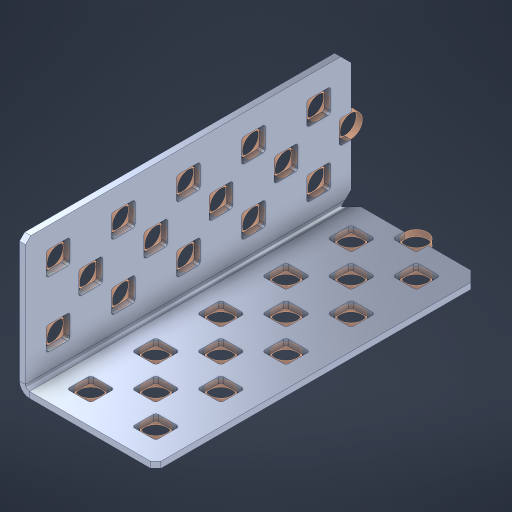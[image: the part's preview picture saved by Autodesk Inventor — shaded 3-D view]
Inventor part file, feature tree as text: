
AUTODESK INVENTOR PART (.ipt)
format: ipt  version: 2023 (Build 270158000, 158)  size: 677,376 bytes
history: native  units: in
note: dims shown in document units (in); Inventor stores cm internally (conversion verified against a paired STEP export)
features: other x36, extrude x28, sheet_metal_op x8, sketch x7, pattern_linear x2, mirror x1, chamfer x1
ambient origin geometry x8: Origin, YZ Plane, XZ Plane, XY Plane, X Axis, Y Axis, Z Axis, Center Point
bodies: Solid1 (feature_tree), Body (feature_tree)
feature tree (83):
  sheet_metal_op  "Flanges"
  sheet_metal_op  "Body Pattern"
  pattern_linear  "Center Pattern"  Spacing1=1.0in  [1 undecoded]
  other  "Arc Length"
  pattern_linear  "Notch Pattern"  Spacing1=0.1875in  [1 undecoded]
  other  "Diagonal Plane"
  mirror  "Everything Mirrored"
  chamfer  "End Chamfer"
  sketch  "Sketch1"  dims[d0=1.0in]
  other  "Plate1"
  sketch  "Sketch2"  dims[d1=2.5in]
  other  "Plate2"
  sheet_metal_op  "Bend1"
  sheet_metal_op  "Corner1"
  sketch  "Sketch8"  dims[d2=0.0469in]
  sketch  "Sketch9"  dims[d3=0.0469in]
  other  "Srf91"
  sheet_metal_op  "Body Pattern Sketch"
  other  "Srf92"
  sketch  "Sketch13"  dims[d4=0.0234in]
  sketch  "Sketch15"  dims[d5=0.0938in]
  sketch  "Sketch16"  dims[d6=0.0469in d7=1.0in d8=90.0deg d9=0.0312in d10=0.1875in d11=0.0469in d12=0.0469in d49=0.182in d50=0.02in d52=0.25in d53=0.0469in d54=0.0in d55=0.172in d56=1.0in d57=0.0in d60=1.9685in d62=0.5in d63=0.7874in d65=0.5in d85=0.1473in d86=0.1659in d89=0.0469in d90=0.0in d91=0.04in d92=0.0491in d95=2.5in d96=0.04in d97=0.25in d98=45.0deg d99=0.25in d106=0.182in d107=0.02in d108=0.5in d110=0.0469in d111=0.0in d112=0.172in d113=0.5in d114=0.0in d117=0.5in d123=0.25in d125=0.25in d126=0.0491in d127=0.1227in d128=0.08in d129=0.04in d130=2.5in]
  other  "Srf786"
  other  "Srf856"
  other  "Srf857"
  other  "Srf858"
  other  "Srf859"
  other  "Srf860"
  other  "Srf861"
  other  "Srf889"
  other  "Srf890"
  other  "Srf891"
  other  "Srf1275"
  other  "Srf1276"
  other  "Srf1278"
  other  "Srf1279"
  other  "Srf1280"
  other  "Srf1281"
  other  "Srf1282"
  other  "Srf1283"
  other  "Srf1277"
  other  "Srf1285"
  other  "Srf1286"
  other  "Srf1287"
  other  "Srf1383"
  other  "Srf1384"
  other  "Srf1445"
  other  "Srf1475"
  other  "Srf1476"
  other  "Srf1537"
  sheet_metal_op  "Body Stamp"
  sheet_metal_op  "Body Circle"
  other  "Center Stamp"
  other  "Center Circle"
  sheet_metal_op  "Notch"
  extrude  "ExtrusionSrf92"  Depth=0.0469in
  extrude  "ExtrusionSrf856"  Depth=0.0469in
  extrude  "ExtrusionSrf857"  Depth=2.5in
  extrude  "ExtrusionSrf858"  Depth=0.02in
  extrude  "ExtrusionSrf859"  Depth=2.5in
  extrude  "ExtrusionSrf860"  Depth=0.0469in
  extrude  "ExtrusionSrf861"  TaperAngle=0.0deg  [1 undecoded]
  extrude  "ExtrusionSrf889"  Depth=2.5in
  extrude  "ExtrusionSrf890"  Depth=1.0in TaperAngle=0.0deg
  extrude  "ExtrusionSrf891"  Depth=2.5in
  extrude  "ExtrusionSrf1275"  Depth=0.5in
  extrude  "ExtrusionSrf1276"  Depth=2.5in
  extrude  "ExtrusionSrf1277"  Depth=2.5in
  extrude  "ExtrusionSrf1278"  Depth=0.0469in
  extrude  "ExtrusionSrf1279"  Depth=2.5in TaperAngle=0.0deg
  extrude  "ExtrusionSrf1280"  Depth=2.5in
  extrude  "ExtrusionSrf1281"  Depth=2.5in TaperAngle=45.0deg
  extrude  "ExtrusionSrf1282"  Depth=2.5in
  extrude  "ExtrusionSrf1345"  Depth=2.5in
  extrude  "ExtrusionSrf1346"  Depth=0.02in
  extrude  "ExtrusionSrf1347"  Depth=0.5in
  extrude  "ExtrusionSrf1348"  Depth=0.0469in
  extrude  "ExtrusionSrf1383"  TaperAngle=0.0deg  [1 undecoded]
  extrude  "ExtrusionSrf1384"  Depth=2.5in
  extrude  "ExtrusionSrf1445"  Depth=0.5in TaperAngle=0.0deg
  extrude  "ExtrusionSrf1475"  Depth=0.5in
  extrude  "ExtrusionSrf1476"  Depth=2.5in
  extrude  "ExtrusionSrf1537"  Depth=2.5in
note: 4 required parameter values undecoded (feature->parameter linkage not recoverable at this tier; creation-order binding heuristic only, values carry confidence <= 0.55)
